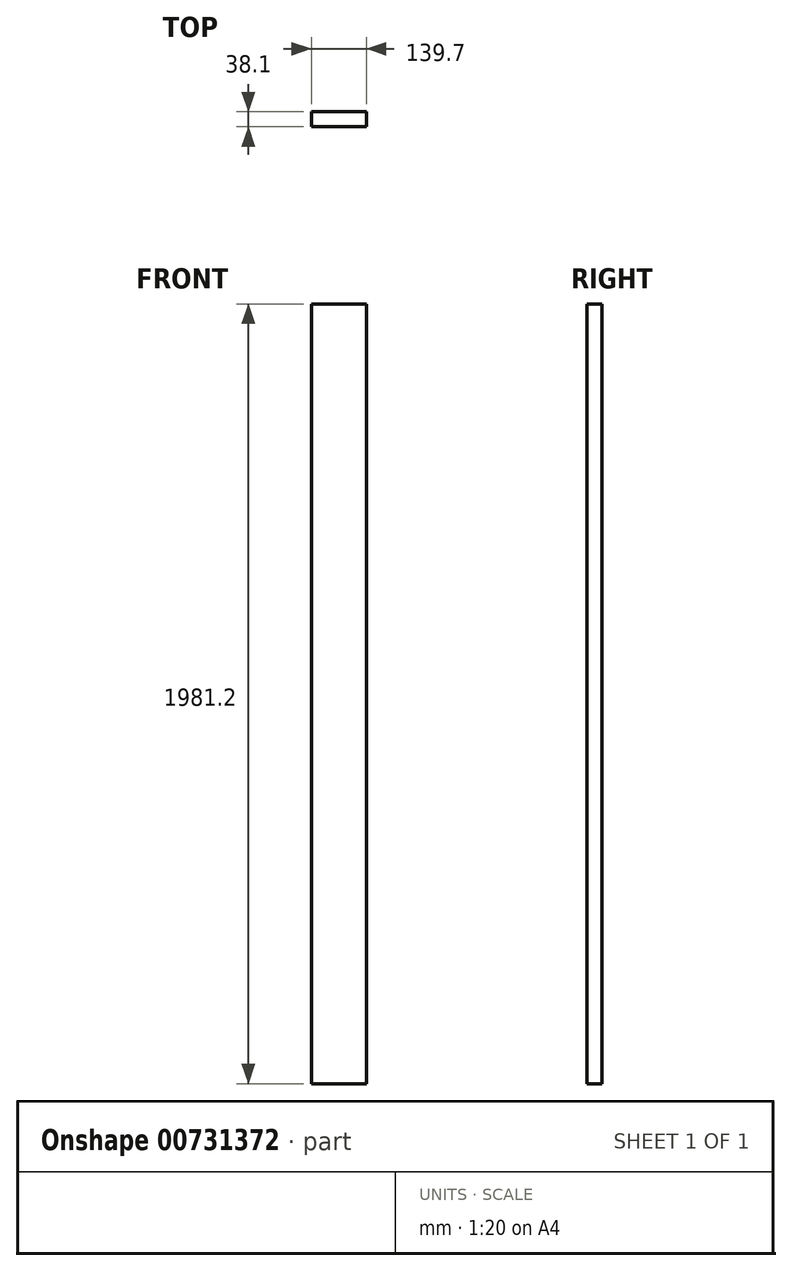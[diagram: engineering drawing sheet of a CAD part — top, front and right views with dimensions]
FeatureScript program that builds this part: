
annotation { "Feature Type Name" : "Feature", "Feature Type Description" : "" }
export const myFeature = defineFeature(function(context is Context, id is Id, definition is map)
    precondition{}
    {
        {
            var Q0;
            Q0=qCreatedBy(makeId("Front.planeOp"),FACE);
            var sketch = newSketch(context, id + "F0", { "sketchPlane" : qUnion([Q0])});
            skLineSegment(sketch, "E0.bottom", {"start": v(69.85, -990.6) * mm, "end": v(-69.85, -990.6) * mm});
            skLineSegment(sketch, "E0.top", {"start": v(69.85, 990.6) * mm, "end": v(-69.85, 990.6) * mm});
            skLineSegment(sketch, "E0.left", {"start": v(69.85, -990.6) * mm, "end": v(69.85, 990.6) * mm});
            skLineSegment(sketch, "E0.right", {"start": v(-69.85, -990.6) * mm, "end": v(-69.85, 990.6) * mm});
            skPoint(sketch, "E0.middle", {"position": v(0, 0) * mm});
            skSolve(sketch);
        }
        {
            var Q0;
            Q0 = qSketchRegion(id + "F0", true);
            extrude(context, id + "F1", {"entities" : qUnion([Q0]), "depth" : 38.1 * mm, "offsetDistance" : 25.4 * mm});
        }
    });
